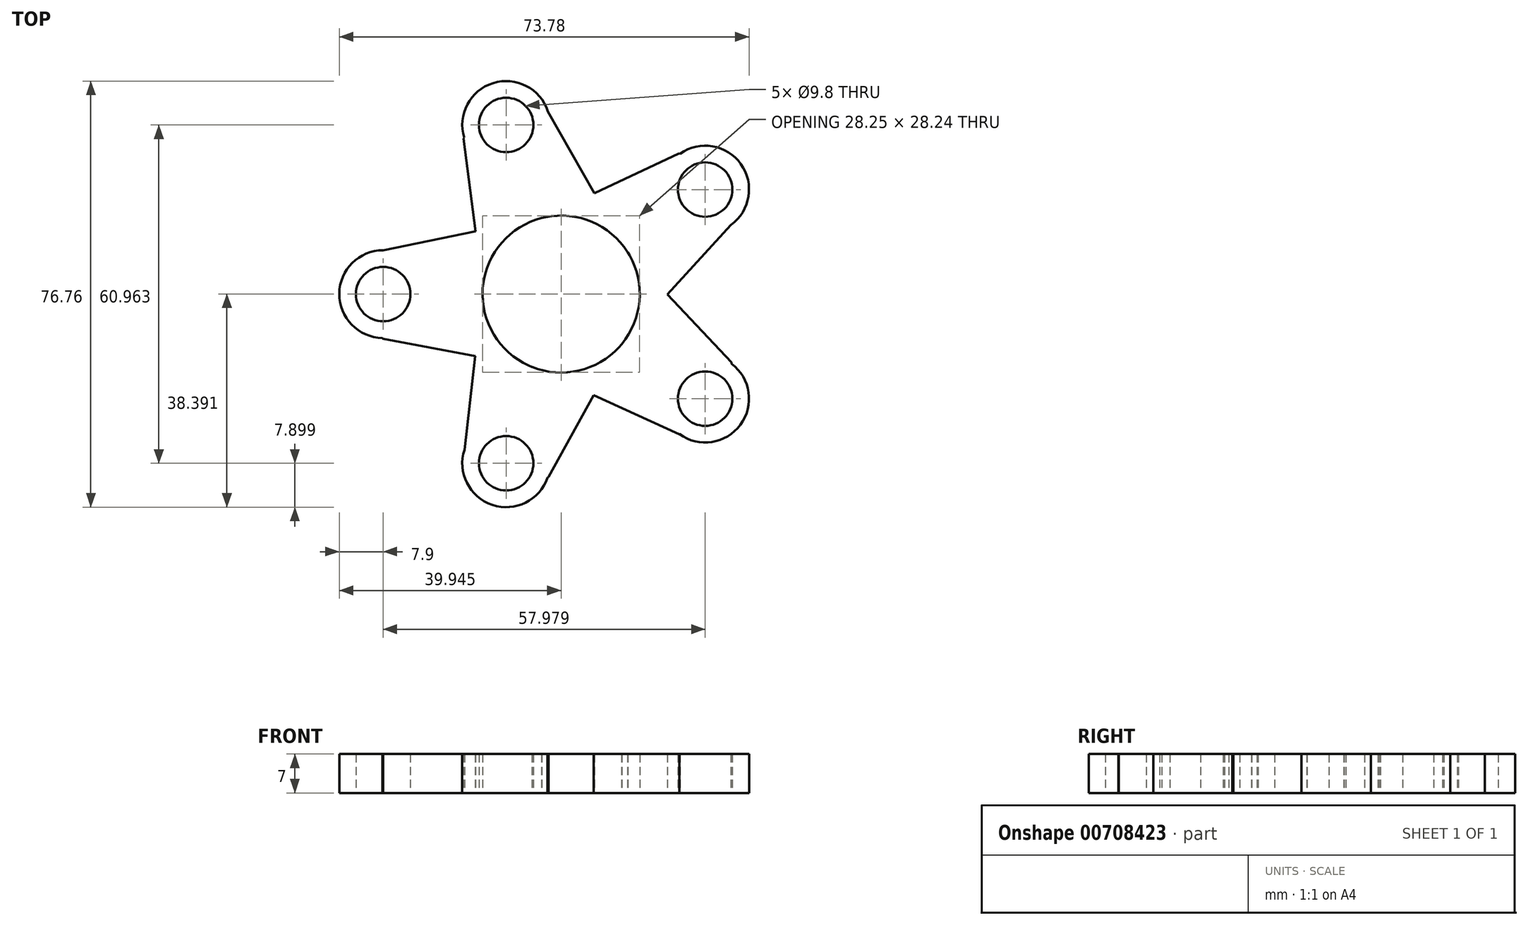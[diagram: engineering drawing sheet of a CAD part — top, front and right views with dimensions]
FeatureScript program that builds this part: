
annotation { "Feature Type Name" : "Feature", "Feature Type Description" : "" }
export const myFeature = defineFeature(function(context is Context, id is Id, definition is map)
    precondition{}
    {
        {
            var Q0;
            Q0=qCreatedBy(makeId("Top.planeOp"),FACE);
            var sketch = newSketch(context, id + "F0", { "sketchPlane" : qUnion([Q0])});
            skCircle(sketch, "E0", {"center": v(0, 0) * mm, "radius": 11.15 * mm});
            skCircle(sketch, "E1", {"center": v(0, 0) * mm, "radius": 14.15 * mm});
            skCircle(sketch, "E2.1.1", {"center": v(-32.05, 0) * mm, "radius": 7.9 * mm});
            skCircle(sketch, "E2.1.2", {"center": v(-32.05, 0) * mm, "radius": 4.9 * mm});
            skLineSegment(sketch, "E3", {"start": v(-32.05, 7.9) * mm, "end": v(0, 14.44) * mm});
            skLineSegment(sketch, "E4", {"start": v(0, -14.15) * mm, "end": v(-32.05, -8.04) * mm});
            skLineSegment(sketch, "E5", {"start": v(-32.05, -8.04) * mm, "end": v(-39.95, 0) * mm});
            skLineSegment(sketch, "E6", {"start": v(-39.95, 0) * mm, "end": v(-32.05, 7.9) * mm});
            skLineSegment(sketch, "E7.1.0", {"start": v(-17.42, -28.04) * mm, "end": v(-13.73, 4.46) * mm});
            skCircle(sketch, "E7.1.1", {"center": v(-9.9, -30.48) * mm, "radius": 7.9 * mm});
            skLineSegment(sketch, "E7.1.2", {"start": v(-2.26, -32.97) * mm, "end": v(-12.35, -38) * mm});
            skLineSegment(sketch, "E7.1.3", {"start": v(-12.35, -38) * mm, "end": v(-17.42, -28.04) * mm});
            skCircle(sketch, "E7.1.4", {"center": v(-9.9, -30.48) * mm, "radius": 4.9 * mm});
            skLineSegment(sketch, "E7.1.5", {"start": v(13.46, -4.37) * mm, "end": v(-2.26, -32.97) * mm});
            skLineSegment(sketch, "E7.2.0", {"start": v(21.29, -25.23) * mm, "end": v(-8.49, -11.68) * mm});
            skCircle(sketch, "E7.2.1", {"center": v(25.93, -18.84) * mm, "radius": 7.9 * mm});
            skLineSegment(sketch, "E7.2.2", {"start": v(30.66, -12.33) * mm, "end": v(32.32, -23.48) * mm});
            skLineSegment(sketch, "E7.2.3", {"start": v(32.32, -23.48) * mm, "end": v(21.29, -25.23) * mm});
            skCircle(sketch, "E7.2.4", {"center": v(25.93, -18.84) * mm, "radius": 4.9 * mm});
            skLineSegment(sketch, "E7.2.5", {"start": v(8.32, 11.45) * mm, "end": v(30.66, -12.33) * mm});
            skLineSegment(sketch, "E7.3.0", {"start": v(30.57, 12.45) * mm, "end": v(8.49, -11.68) * mm});
            skCircle(sketch, "E7.3.1", {"center": v(25.93, 18.84) * mm, "radius": 7.9 * mm});
            skLineSegment(sketch, "E7.3.2", {"start": v(21.2, 25.34) * mm, "end": v(32.32, 23.48) * mm});
            skLineSegment(sketch, "E7.3.3", {"start": v(32.32, 23.48) * mm, "end": v(30.57, 12.45) * mm});
            skCircle(sketch, "E7.3.4", {"center": v(25.93, 18.84) * mm, "radius": 4.9 * mm});
            skLineSegment(sketch, "E7.3.5", {"start": v(-8.32, 11.45) * mm, "end": v(21.2, 25.34) * mm});
            skLineSegment(sketch, "E7.4.0", {"start": v(-2.4, 32.92) * mm, "end": v(13.73, 4.46) * mm});
            skCircle(sketch, "E7.4.1", {"center": v(-9.9, 30.48) * mm, "radius": 7.9 * mm});
            skLineSegment(sketch, "E7.4.2", {"start": v(-17.55, 28) * mm, "end": v(-12.35, 38) * mm});
            skLineSegment(sketch, "E7.4.3", {"start": v(-12.35, 38) * mm, "end": v(-2.4, 32.92) * mm});
            skCircle(sketch, "E7.4.4", {"center": v(-9.9, 30.48) * mm, "radius": 4.9 * mm});
            skLineSegment(sketch, "E7.4.5", {"start": v(-13.46, -4.37) * mm, "end": v(-17.55, 28) * mm});
            skSolve(sketch);
        }
        {
            var Q0;
            Q0 = qSketchRegion(id + "F0", true);
            extrude(context, id + "F1", {"entities" : qUnion([Q0]), "depth" : 7 * mm, "offsetDistance" : 25 * mm});
        }
    });
